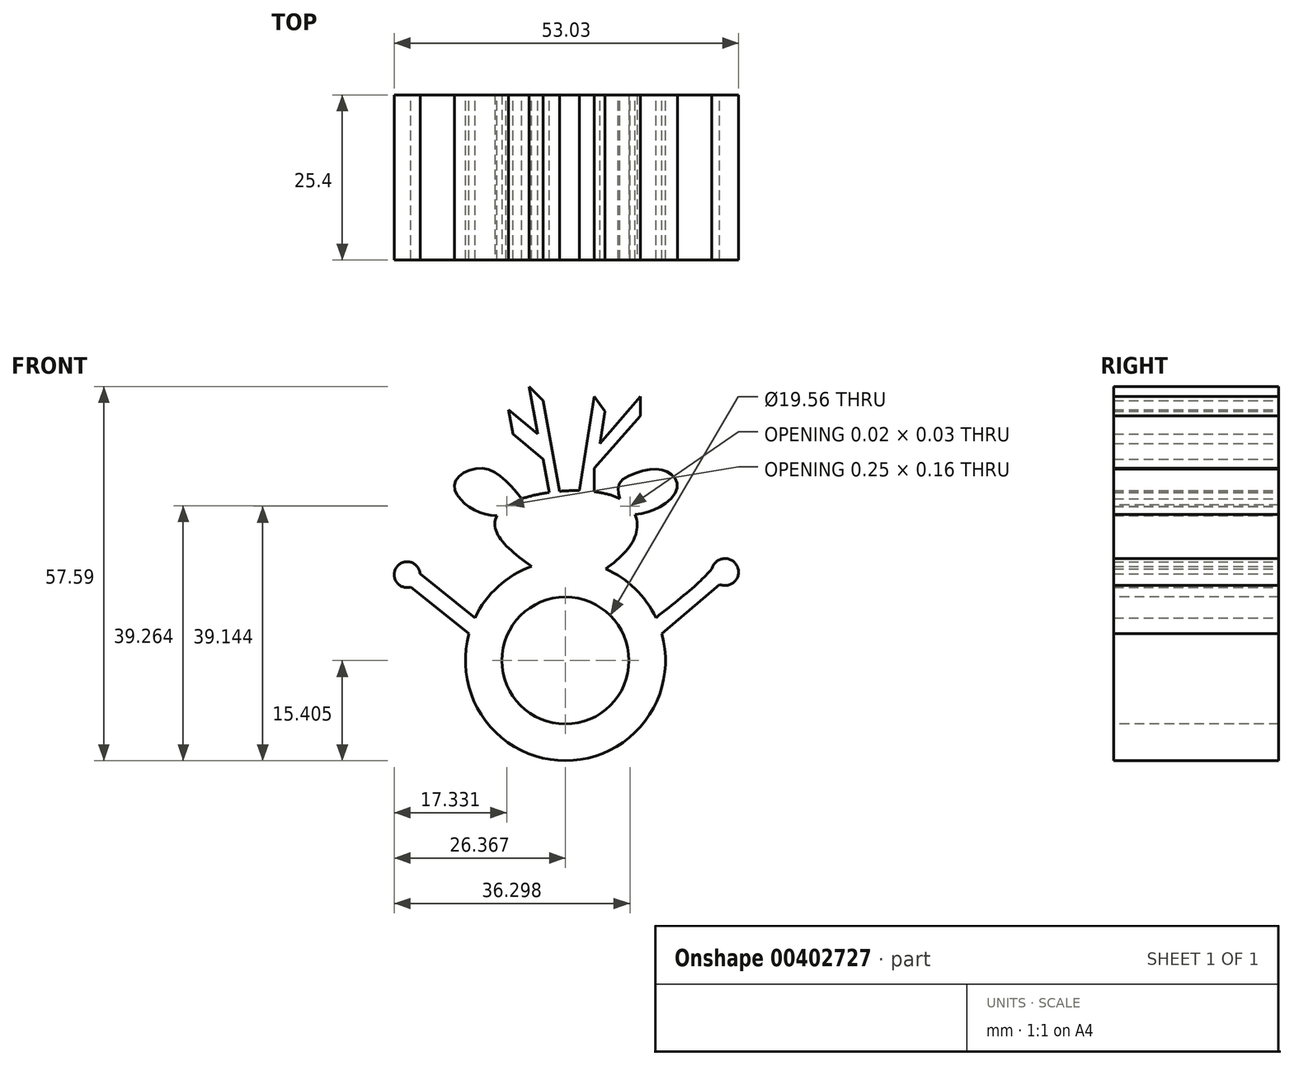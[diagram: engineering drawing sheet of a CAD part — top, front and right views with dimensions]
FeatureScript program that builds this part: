
annotation { "Feature Type Name" : "Feature", "Feature Type Description" : "" }
export const myFeature = defineFeature(function(context is Context, id is Id, definition is map)
    precondition{}
    {
        {
            var Q0;
            Q0=qCreatedBy(makeId("Front.planeOp"),FACE);
            var sketch = newSketch(context, id + "F0", { "sketchPlane" : qUnion([Q0])});
            skCircle(sketch, "E0", {"center": v(0, 7.57) * mm, "radius": 2 * mm});
            skFitSpline(sketch, "E1", {"points": [v(-2, 7.57) * mm, v(-11.45, 15.52) * mm, v(-9.81, 19.8) * mm, v(7.48, 20.77) * mm, v(9.82, 14.96) * mm, v(2, 7.57) * mm], "startDerivative": vector(-54.6, 37.14) * mm, "endDerivative": vector(-47, -34.12) * mm});
            skArc(sketch, "E2", {"start": v(-6.1, 10.36) * mm, "mid": v(-11.25, 7.27) * mm, "end": v(-14.83, 2.44) * mm});
            skFitSpline(sketch, "E3", {"points": [v(9.04, 19.58) * mm, v(11.82, 20.89) * mm, v(13, 23.06) * mm, v(10.25, 22.86) * mm, v(9.04, 19.58) * mm]});
            skFitSpline(sketch, "E4", {"points": [v(-9.81, 19.8) * mm, v(-13.6, 20.77) * mm, v(-15.18, 23.25) * mm, v(-12.22, 22.66) * mm, v(-9.81, 19.8) * mm]});
            skFitSpline(sketch, "E5", {"points": [v(-11.45, 18.17) * mm, v(-16.13, 19.8) * mm, v(-17.94, 23.25) * mm, v(-13.6, 25.44) * mm, v(-7.64, 20.77) * mm], "startDerivative": vector(-22.31, 1.06) * mm, "endDerivative": vector(18.29, -22.45) * mm});
            skFitSpline(sketch, "E6", {"points": [v(9.82, 18.34) * mm, v(13.79, 19.58) * mm, v(16.36, 22.66) * mm, v(14.98, 24.83) * mm, v(11.82, 25.23) * mm, v(7.48, 23.25) * mm, v(7.48, 20.77) * mm], "startDerivative": vector(22.93, 2.8) * mm, "endDerivative": vector(5.23, -19.16) * mm});
            skCircle(sketch, "E7", {"center": v(-2.55, 12.41) * mm, "radius": 1.23 * mm});
            skCircle(sketch, "E8", {"center": v(1.62, 12.23) * mm, "radius": 1.17 * mm});
            skFitSpline(sketch, "E9", {"points": [v(-3.97, 8.9) * mm, v(-11.45, 0) * mm, v(-11.45, -7.83) * mm, v(-9.07, -13.8) * mm, v(-6.1, -9.66) * mm, v(-2, -16) * mm, v(0, -10.64) * mm, v(5.91, -14.59) * mm, v(6.3, -7.3) * mm, v(10.05, -9.86) * mm, v(10.25, -3.55) * mm, v(12.02, -5.13) * mm, v(10.67, 2.44) * mm, v(3.26, 8.48) * mm], "startDerivative": vector(-89.15, -90.92) * mm, "endDerivative": vector(-94.4, 42.98) * mm});
            skFitSpline(sketch, "E10", {"points": [v(13.03, 2.44) * mm, v(19.29, 7.57) * mm, v(21.65, 9.96) * mm], "startDerivative": vector(11.3, 9.18) * mm, "endDerivative": vector(5.23, 5.5) * mm});
            skLineSegment(sketch, "E11", {"start": v(1.22, 22.01) * mm, "end": v(3.55, 36.49) * mm});
            skLineSegment(sketch, "E12", {"start": v(3.55, 36.49) * mm, "end": v(5.2, 34.22) * mm});
            skLineSegment(sketch, "E13", {"start": v(5.2, 34.22) * mm, "end": v(4.4, 29.25) * mm});
            skPoint(sketch, "E13.endSnap0", {"position": v(2.39, 29.25) * mm});
            skLineSegment(sketch, "E14", {"start": v(4.4, 29.25) * mm, "end": v(10.64, 36.49) * mm});
            skLineSegment(sketch, "E15", {"start": v(10.64, 36.49) * mm, "end": v(10.64, 33.52) * mm});
            skLineSegment(sketch, "E16", {"start": v(10.64, 33.52) * mm, "end": v(3.55, 25.44) * mm});
            skLineSegment(sketch, "E17", {"start": v(3.55, 25.44) * mm, "end": v(3.55, 21.85) * mm});
            skLineSegment(sketch, "E18", {"start": v(-1.78, 21.92) * mm, "end": v(-4.34, 35.9) * mm});
            skLineSegment(sketch, "E19", {"start": v(-4.34, 35.9) * mm, "end": v(-6.5, 38.04) * mm});
            skLineSegment(sketch, "E20", {"start": v(-6.5, 38.04) * mm, "end": v(-5.17, 30.74) * mm});
            skLineSegment(sketch, "E21", {"start": v(-5.17, 30.74) * mm, "end": v(-9.66, 34.49) * mm});
            skLineSegment(sketch, "E22", {"start": v(-9.66, 34.49) * mm, "end": v(-8.97, 30.74) * mm});
            skLineSegment(sketch, "E23", {"start": v(-8.97, 30.74) * mm, "end": v(-4.34, 26.83) * mm});
            skLineSegment(sketch, "E24", {"start": v(-4.34, 26.83) * mm, "end": v(-3.4, 21.74) * mm});
            skLineSegment(sketch, "E25", {"start": v(13.93, 0) * mm, "end": v(22.85, 7.57) * mm});
            skLineSegment(sketch, "E26", {"start": v(-14.83, 2.44) * mm, "end": v(-23.29, 9.24) * mm});
            skLineSegment(sketch, "E27", {"start": v(-24.75, 7.16) * mm, "end": v(-15.74, 0) * mm});
            skArc(sketch, "E28", {"start": v(-23.29, 9.24) * mm, "mid": v(-26.9, 10.23) * mm, "end": v(-24.75, 7.16) * mm});
            skArc(sketch, "E29", {"start": v(22.85, 7.57) * mm, "mid": v(25.53, 10.42) * mm, "end": v(21.65, 9.96) * mm});
            skArc(sketch, "E30.trimOffspring", {"start": v(-15.74, 0) * mm, "mid": v(-0.9, -19.55) * mm, "end": v(13.93, 0) * mm});
            skArc(sketch, "E31.trimOffspring", {"start": v(13.03, 2.44) * mm, "mid": v(9.84, 6.9) * mm, "end": v(5.3, 9.96) * mm});
            skSolve(sketch);
        }
        {
            var Q0;
            Q0=makeQuery(id+"F0.imprint","IMPRINT",FACE,{"disambiguationData":[TD([[makeQuery(id+"F0.imprint","IMPRINT",EDGE,{"derivedFrom":sQuery(id+"F0.wireOp",EDGE,"E7")}),-1.0]])]});
            var Q1;
            {var subQ0=sQuery(id+"F0.wireOp",EDGE,"E1");var subQ1=sQuery(id+"F0.wireOp",EDGE,"E0");var subQ2=makeQuery(id+"F0.imprint","INTERSECT",VERTEX,{"disambiguationData":[OD(0.0)],"derivedFrom":[subQ1,subQ0]});Q1=makeQuery(id+"F0.imprint","IMPRINT",FACE,{"disambiguationData":[TD([[makeQuery(id+"F0.imprint","IMPRINT",EDGE,{"disambiguationData":[TD([[subQ2,1.0]])],"derivedFrom":subQ1}),1.0]])]});}
            var Q2;
            {var subQ0=sQuery(id+"F0.wireOp",EDGE,"E5");Q2=makeQuery(id+"F0.imprint","IMPRINT",FACE,{"disambiguationData":[TD([[makeQuery(id+"F0.imprint","IMPRINT",EDGE,{"derivedFrom":subQ0}),-1.0]])]});}
            var Q3;
            {var subQ0=sQuery(id+"F0.wireOp",EDGE,"E18");Q3=makeQuery(id+"F0.imprint","IMPRINT",FACE,{"disambiguationData":[TD([[makeQuery(id+"F0.imprint","IMPRINT",EDGE,{"derivedFrom":subQ0}),1.0]])]});}
            var Q4;
            {var subQ0=sQuery(id+"F0.wireOp",EDGE,"E4");var subQ1=sQuery(id+"F0.wireOp",EDGE,"E1");var subQ2=makeQuery(id+"F0.imprint","INTERSECT",VERTEX,{"disambiguationData":[OD(0.0)],"derivedFrom":[subQ1,subQ0]});Q4=makeQuery(id+"F0.imprint","IMPRINT",FACE,{"disambiguationData":[TD([[makeQuery(id+"F0.imprint","IMPRINT",EDGE,{"disambiguationData":[TD([[subQ2,-1.0]])],"derivedFrom":subQ1}),1.0]])]});}
            var Q5;
            {var subQ0=sQuery(id+"F0.wireOp",EDGE,"E11");Q5=makeQuery(id+"F0.imprint","IMPRINT",FACE,{"disambiguationData":[TD([[makeQuery(id+"F0.imprint","IMPRINT",EDGE,{"derivedFrom":subQ0}),-1.0]])]});}
            var Q6;
            {var subQ0=sQuery(id+"F0.wireOp",EDGE,"E6");Q6=makeQuery(id+"F0.imprint","IMPRINT",FACE,{"disambiguationData":[TD([[makeQuery(id+"F0.imprint","IMPRINT",EDGE,{"derivedFrom":subQ0}),1.0]])]});}
            var Q7;
            {var subQ0=sQuery(id+"F0.wireOp",EDGE,"E3");var subQ1=sQuery(id+"F0.wireOp",EDGE,"E1");var subQ2=makeQuery(id+"F0.imprint","INTERSECT",VERTEX,{"disambiguationData":[OD(0.0)],"derivedFrom":[subQ1,subQ0]});Q7=makeQuery(id+"F0.imprint","IMPRINT",FACE,{"disambiguationData":[TD([[makeQuery(id+"F0.imprint","IMPRINT",EDGE,{"disambiguationData":[TD([[subQ2,1.0]])],"derivedFrom":subQ0}),1.0]])]});}
            var Q8;
            Q8=makeQuery(id+"F0.imprint","IMPRINT",FACE,{"disambiguationData":[TD([[makeQuery(id+"F0.imprint","IMPRINT",EDGE,{"derivedFrom":sQuery(id+"F0.wireOp",EDGE,"LyWLNa7e-lTLL-S35t-eIR6-l8GTtOQRgtLx")}),-1.0]])]});
            var Q9;
            Q9=makeQuery(id+"F0.imprint","IMPRINT",FACE,{"disambiguationData":[TD([[makeQuery(id+"F0.imprint","IMPRINT",EDGE,{"derivedFrom":sQuery(id+"F0.wireOp",EDGE,"WiR8fL2Q-7bwI-CRjU-9ThL-zh9Lgz0hX4EA")}),-1.0]])]});
            var Q10;
            Q10=makeQuery(id+"F0.imprint","IMPRINT",FACE,{"disambiguationData":[TD([[makeQuery(id+"F0.imprint","IMPRINT",EDGE,{"derivedFrom":sQuery(id+"F0.wireOp",EDGE,"E8")}),1.0]])]});
            var Q11;
            Q11=makeQuery(id+"F0.imprint","IMPRINT",FACE,{"disambiguationData":[TD([[makeQuery(id+"F0.imprint","IMPRINT",EDGE,{"derivedFrom":sQuery(id+"F0.wireOp",EDGE,"E7")}),1.0]])]});
            var Q12;
            {var subQ4=sQuery(id+"F0.wireOp",EDGE,"E9");Q12=makeQuery(id+"F0.imprint","IMPRINT",FACE,{"disambiguationData":[TD([[makeQuery(id+"F0.imprint","IMPRINT",EDGE,{"derivedFrom":subQ4}),1.0]])]});}
            var Q13;
            {var subQ0=sQuery(id+"F0.wireOp",EDGE,"E2");Q13=makeQuery(id+"F0.imprint","IMPRINT",FACE,{"disambiguationData":[TD([[makeQuery(id+"F0.imprint","IMPRINT",EDGE,{"derivedFrom":subQ0}),1.0]])]});}
            extrude(context, id + "F1", {"entities" : qUnion([Q0, Q1, Q2, Q3, Q4, Q5, Q6, Q7, Q8, Q9, Q10, Q11, Q12, Q13]), "depth" : 25.4 * mm});
        }
        {
            var Q0;
            Q0=makeQuery(id+"F1.opExtrude","CAP_FACE",FACE,{"disambiguationData":[OSD([sQuery(id+"F0.wireOp",EDGE,"E1"),sQuery(id+"F0.wireOp",EDGE,"E2"),sQuery(id+"F0.wireOp",EDGE,"E3"),sQuery(id+"F0.wireOp",EDGE,"E4"),sQuery(id+"F0.wireOp",EDGE,"E5"),sQuery(id+"F0.wireOp",EDGE,"E6"),sQuery(id+"F0.wireOp",EDGE,"E10"),sQuery(id+"F0.wireOp",EDGE,"E11"),sQuery(id+"F0.wireOp",EDGE,"E12"),sQuery(id+"F0.wireOp",EDGE,"E13"),sQuery(id+"F0.wireOp",EDGE,"E14"),sQuery(id+"F0.wireOp",EDGE,"E15"),sQuery(id+"F0.wireOp",EDGE,"E16"),sQuery(id+"F0.wireOp",EDGE,"E17"),sQuery(id+"F0.wireOp",EDGE,"E18"),sQuery(id+"F0.wireOp",EDGE,"E19"),sQuery(id+"F0.wireOp",EDGE,"E20"),sQuery(id+"F0.wireOp",EDGE,"E21"),sQuery(id+"F0.wireOp",EDGE,"E22"),sQuery(id+"F0.wireOp",EDGE,"E23"),sQuery(id+"F0.wireOp",EDGE,"E24"),sQuery(id+"F0.wireOp",EDGE,"E25"),sQuery(id+"F0.wireOp",EDGE,"E26"),sQuery(id+"F0.wireOp",EDGE,"E27"),sQuery(id+"F0.wireOp",EDGE,"E28"),sQuery(id+"F0.wireOp",EDGE,"E29"),sQuery(id+"F0.wireOp",EDGE,"E30.trimOffspring"),sQuery(id+"F0.wireOp",EDGE,"E31.trimOffspring")])],"isStart":false});
            var sketch = newSketch(context, id + "F2", { "sketchPlane" : qUnion([Q0])});
            skCircle(sketch, "E32", {"center": v(-0.9, -4.15) * mm, "radius": 9.78 * mm});
            skSolve(sketch);
        }
        {
            var Q0;
            Q0 = qSketchRegion(id + "F2", true);
            var Q1;
            Q1=sQuery(id+"F2.wireOp",EDGE,"E32");
            extrude(context, id + "F3", {"entities" : qUnion([Q0]), "operationType" : NewBodyOperationType.REMOVE, "surfaceEntities" : qUnion([Q1]), "endBound" : BoundingType.THROUGH_ALL, "oppositeDirection" : true, "depth" : 25.4 * mm});
        }
    });
